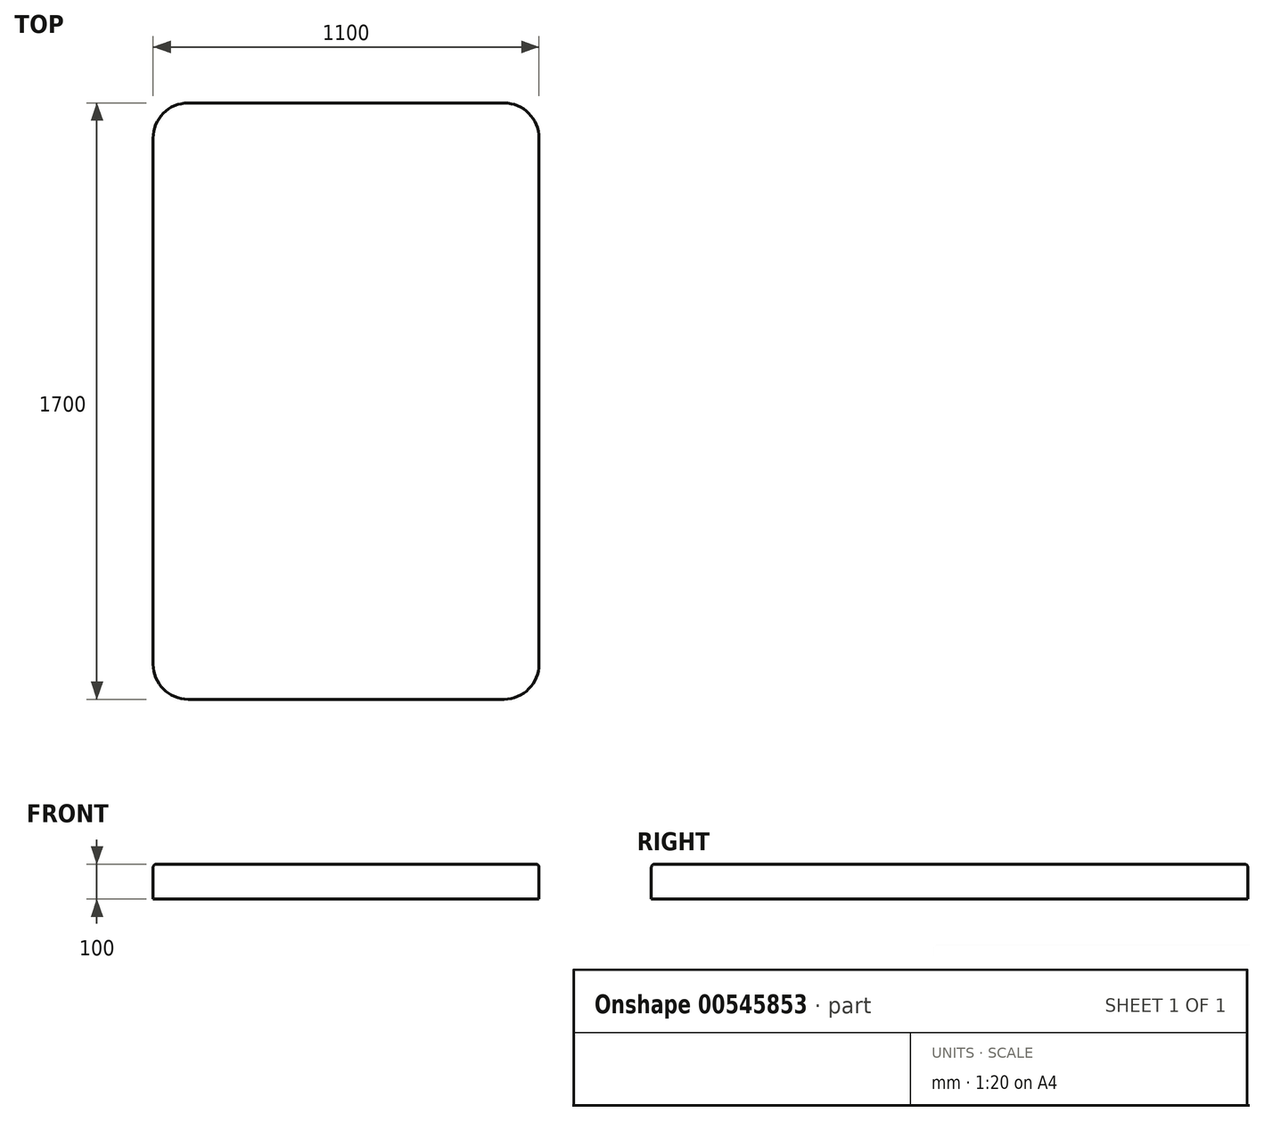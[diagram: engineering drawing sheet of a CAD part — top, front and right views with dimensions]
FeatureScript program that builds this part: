
annotation { "Feature Type Name" : "Feature", "Feature Type Description" : "" }
export const myFeature = defineFeature(function(context is Context, id is Id, definition is map)
    precondition{}
    {
        {
            var Q0;
            Q0=qCreatedBy(makeId("Top.planeOp"),FACE);
            var sketch = newSketch(context, id + "F0", { "sketchPlane" : qUnion([Q0])});
            skLineSegment(sketch, "E0.bottom", {"start": v(0, 0) * mm, "end": v(1100, 0) * mm});
            skLineSegment(sketch, "E0.top", {"start": v(0, -1700) * mm, "end": v(1100, -1700) * mm});
            skLineSegment(sketch, "E0.left", {"start": v(0, 0) * mm, "end": v(0, -1700) * mm});
            skLineSegment(sketch, "E0.right", {"start": v(1100, 0) * mm, "end": v(1100, -1700) * mm});
            skSolve(sketch);
        }
        {
            var Q0;
            Q0 = qSketchRegion(id + "F0", true);
            extrude(context, id + "F1", {"entities" : qUnion([Q0]), "depth" : 100 * mm, "offsetDistance" : 25 * mm});
        }
        {
            var Q0;
            Q0=makeQuery(id+"F1.opExtrude","SWEPT_EDGE",EDGE,{"disambiguationData":[OSD([sQuery(id+"F0.wireOp",EDGE,"E0.top"),sQuery(id+"F0.wireOp",EDGE,"E0.left")])]});
            var Q1;
            Q1=makeQuery(id+"F1.opExtrude","SWEPT_EDGE",EDGE,{"disambiguationData":[OSD([sQuery(id+"F0.wireOp",EDGE,"E0.top"),sQuery(id+"F0.wireOp",EDGE,"E0.right")])]});
            var Q2;
            Q2=makeQuery(id+"F1.opExtrude","SWEPT_EDGE",EDGE,{"disambiguationData":[OSD([sQuery(id+"F0.wireOp",EDGE,"E0.bottom"),sQuery(id+"F0.wireOp",EDGE,"E0.right")])]});
            var Q3;
            Q3=makeQuery(id+"F1.opExtrude","SWEPT_EDGE",EDGE,{"disambiguationData":[OSD([sQuery(id+"F0.wireOp",EDGE,"E0.bottom"),sQuery(id+"F0.wireOp",EDGE,"E0.left")])]});
            fillet(context, id + "F2", {"entities" : qUnion([Q0, Q1, Q2, Q3]), "radius" : 100 * mm, "tangentPropagation" : true, "allowEdgeOverflow" : false});
        }
        {
            var Q0;
            Q0=makeQuery(id+"F1.opExtrude","CAP_FACE",FACE,{"disambiguationData":[OSD([sQuery(id+"F0.wireOp",EDGE,"E0.bottom"),sQuery(id+"F0.wireOp",EDGE,"E0.top"),sQuery(id+"F0.wireOp",EDGE,"E0.left"),sQuery(id+"F0.wireOp",EDGE,"E0.right")])],"isStart":false});
            fillet(context, id + "F3", {"entities" : qUnion([Q0]), "radius" : 10 * mm, "tangentPropagation" : true, "allowEdgeOverflow" : false});
        }
    });
